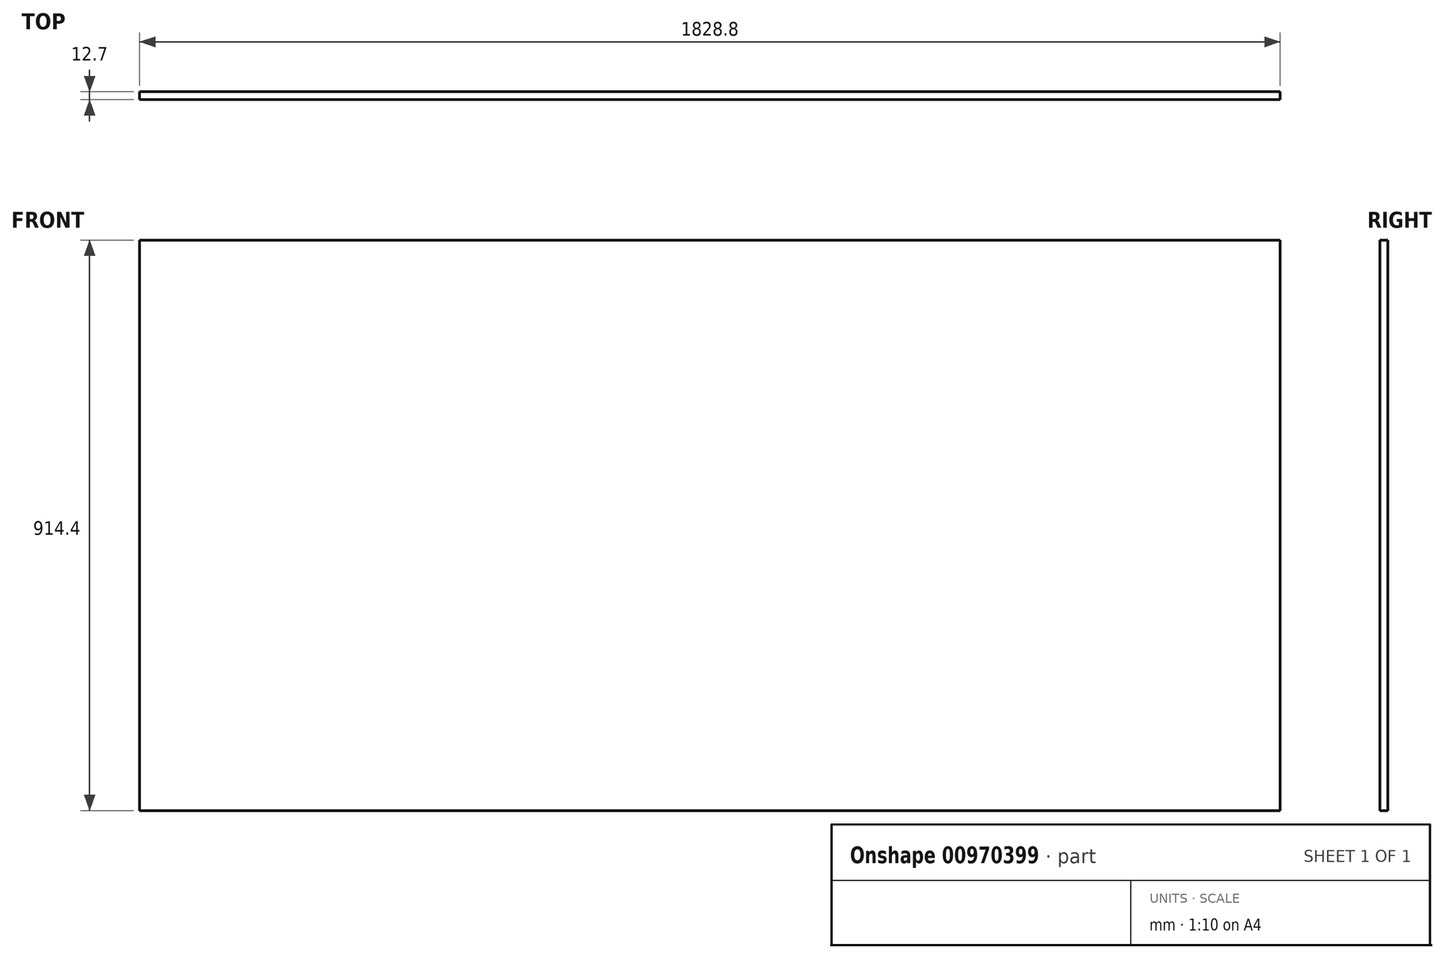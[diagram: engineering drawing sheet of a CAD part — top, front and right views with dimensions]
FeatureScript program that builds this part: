
annotation { "Feature Type Name" : "Feature", "Feature Type Description" : "" }
export const myFeature = defineFeature(function(context is Context, id is Id, definition is map)
    precondition{}
    {
        {
            var Q0;
            Q0=qCreatedBy(makeId("Front.planeOp"),FACE);
            var sketch = newSketch(context, id + "F0", { "sketchPlane" : qUnion([Q0])});
            skLineSegment(sketch, "E0.bottom", {"start": v(0, 0) * mm, "end": v(1828.8, 0) * mm});
            skLineSegment(sketch, "E0.top", {"start": v(0, -914.4) * mm, "end": v(1828.8, -914.4) * mm});
            skLineSegment(sketch, "E0.left", {"start": v(0, 0) * mm, "end": v(0, -914.4) * mm});
            skLineSegment(sketch, "E0.right", {"start": v(1828.8, 0) * mm, "end": v(1828.8, -914.4) * mm});
            skSolve(sketch);
        }
        {
            var Q0;
            Q0 = qSketchRegion(id + "F0", true);
            extrude(context, id + "F1", {"entities" : qUnion([Q0]), "depth" : 12.7 * mm, "offsetDistance" : 25.4 * mm});
        }
    });
